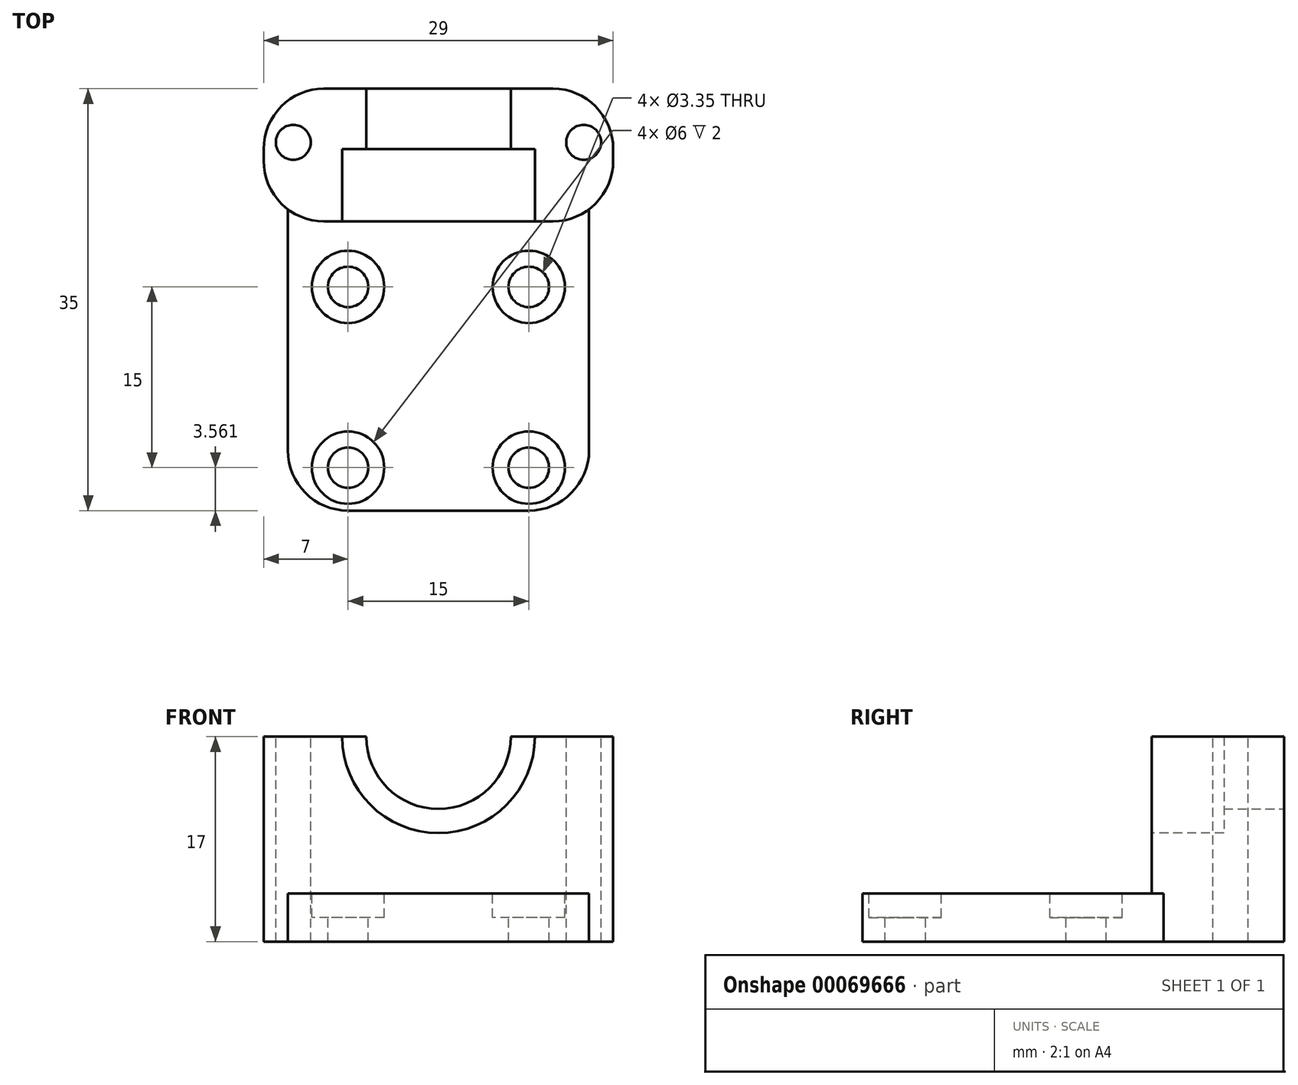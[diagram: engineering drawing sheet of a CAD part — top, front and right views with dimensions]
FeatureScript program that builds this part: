
annotation { "Feature Type Name" : "Feature", "Feature Type Description" : "" }
export const myFeature = defineFeature(function(context is Context, id is Id, definition is map)
    precondition{}
    {
        {
            var Q0;
            Q0=qCreatedBy(makeId("Top.planeOp"),FACE);
            var sketch = newSketch(context, id + "F0", { "sketchPlane" : qUnion([Q0])});
            skLineSegment(sketch, "E0.bottom", {"start": v(0, 0) * mm, "end": v(25, 0) * mm});
            skLineSegment(sketch, "E0.top", {"start": v(0, 35) * mm, "end": v(25, 35) * mm});
            skLineSegment(sketch, "E0.left", {"start": v(0, 0) * mm, "end": v(0, 35) * mm});
            skLineSegment(sketch, "E0.right", {"start": v(25, 0) * mm, "end": v(25, 35) * mm});
            skSolve(sketch);
        }
        {
            var Q0;
            Q0=qSketchRegion(id+"F0",true);
            extrude(context, id + "F1", {"entities" : qUnion([Q0]), "depth" : 4 * mm});
        }
        {
            var Q0;
            Q0=makeQuery(id+"F1.opExtrude","CAP_FACE",FACE,{"disambiguationData":[OSD([sQuery(id+"F0.wireOp",EDGE,"E0.bottom"),sQuery(id+"F0.wireOp",EDGE,"E0.top"),sQuery(id+"F0.wireOp",EDGE,"E0.left"),sQuery(id+"F0.wireOp",EDGE,"E0.right")])],"isStart":false});
            var sketch = newSketch(context, id + "F2", { "sketchPlane" : qUnion([Q0])});
            skCircle(sketch, "E1", {"center": v(5, 18.56) * mm, "radius": 1.68 * mm});
            skCircle(sketch, "E2", {"center": v(20, 18.56) * mm, "radius": 1.68 * mm});
            skCircle(sketch, "E3", {"center": v(5, 3.56) * mm, "radius": 1.68 * mm});
            skCircle(sketch, "E4", {"center": v(20, 3.56) * mm, "radius": 1.68 * mm});
            skLineSegment(sketch, "E5", {"start": v(5, 18.56) * mm, "end": v(0, 18.56) * mm});
            skLineSegment(sketch, "E6", {"start": v(20, 3.56) * mm, "end": v(25, 3.56) * mm});
            skCircle(sketch, "E7", {"center": v(5, 18.56) * mm, "radius": 3 * mm});
            skCircle(sketch, "E8", {"center": v(20, 18.56) * mm, "radius": 3 * mm});
            skCircle(sketch, "E9", {"center": v(5, 3.56) * mm, "radius": 3 * mm});
            skCircle(sketch, "E10", {"center": v(20, 3.56) * mm, "radius": 3 * mm});
            skSolve(sketch);
        }
        {
            var Q0;
            Q0=makeQuery(id+"F2.imprint","IMPRINT",FACE,{"disambiguationData":[TD([[makeQuery(id+"F2.imprint","IMPRINT",EDGE,{"derivedFrom":sQuery(id+"F2.wireOp",EDGE,"E1")}),1.0]])]});
            var Q1;
            Q1=makeQuery(id+"F2.imprint","IMPRINT",FACE,{"disambiguationData":[TD([[makeQuery(id+"F2.imprint","IMPRINT",EDGE,{"derivedFrom":sQuery(id+"F2.wireOp",EDGE,"E2")}),1.0]])]});
            var Q2;
            Q2=makeQuery(id+"F2.imprint","IMPRINT",FACE,{"disambiguationData":[TD([[makeQuery(id+"F2.imprint","IMPRINT",EDGE,{"derivedFrom":sQuery(id+"F2.wireOp",EDGE,"E4")}),1.0]])]});
            var Q3;
            Q3=makeQuery(id+"F2.imprint","IMPRINT",FACE,{"disambiguationData":[TD([[makeQuery(id+"F2.imprint","IMPRINT",EDGE,{"derivedFrom":sQuery(id+"F2.wireOp",EDGE,"E3")}),1.0]])]});
            extrude(context, id + "F3", {"entities" : qUnion([Q0, Q1, Q2, Q3]), "operationType" : NewBodyOperationType.REMOVE, "oppositeDirection" : true, "depth" : 25 * mm});
        }
        {
            var Q0;
            Q0=makeQuery(id+"F1.opExtrude","CAP_FACE",FACE,{"disambiguationData":[OSD([sQuery(id+"F0.wireOp",EDGE,"E0.bottom"),sQuery(id+"F0.wireOp",EDGE,"E0.top"),sQuery(id+"F0.wireOp",EDGE,"E0.left"),sQuery(id+"F0.wireOp",EDGE,"E0.right")])],"isStart":false});
            var sketch = newSketch(context, id + "F4", { "sketchPlane" : qUnion([Q0])});
            skLineSegment(sketch, "E11.bottom", {"start": v(0, 35) * mm, "end": v(25, 35) * mm});
            skLineSegment(sketch, "E11.top", {"start": v(0, 24) * mm, "end": v(25, 24) * mm});
            skLineSegment(sketch, "E11.left", {"start": v(0, 35) * mm, "end": v(0, 24) * mm});
            skLineSegment(sketch, "E11.right", {"start": v(25, 35) * mm, "end": v(25, 24) * mm});
            skSolve(sketch);
        }
        {
            var Q0;
            Q0=qSketchRegion(id+"F4",true);
            extrude(context, id + "F5", {"entities" : qUnion([Q0]), "operationType" : NewBodyOperationType.ADD, "depth" : 13 * mm});
        }
        {
            var Q0;
            Q0=makeQuery(id+"F5.boolean.opBoolean","MERGE",FACE,{"derivedFrom":[makeQuery(id+"F1.opExtrude","SWEPT_FACE",FACE,{"disambiguationData":[OSD([sQuery(id+"F0.wireOp",EDGE,"E0.top")])]}),makeQuery(id+"F5.opExtrude","SWEPT_FACE",FACE,{"disambiguationData":[OSD([sQuery(id+"F4.wireOp",EDGE,"E11.bottom")])]})]});
            var sketch = newSketch(context, id + "F6", { "sketchPlane" : qUnion([Q0])});
            skCircle(sketch, "E12", {"center": v(-12.5, 17) * mm, "radius": 6 * mm});
            skSolve(sketch);
        }
        {
            var Q0;
            {var subQ0=makeQuery(id+"F5.opExtrude","CAP_EDGE",EDGE,{"disambiguationData":[OSD([sQuery(id+"F4.wireOp",EDGE,"E11.bottom")])],"isStart":false});var subQ1=sQuery(id+"F6.wireOp",EDGE,"E12");var subQ3=makeQuery(id+"F6.imprint","INTERSECT",VERTEX,{"disambiguationData":[OD(0.0)],"derivedFrom":[subQ0,subQ1]});Q0=makeQuery(id+"F6.imprint","IMPRINT",FACE,{"disambiguationData":[TD([[makeQuery(id+"F6.imprint","IMPRINT",EDGE,{"disambiguationData":[TD([[subQ3,1.0]])],"derivedFrom":subQ1}),1.0]])]});}
            extrude(context, id + "F7", {"entities" : qUnion([Q0]), "operationType" : NewBodyOperationType.REMOVE, "oppositeDirection" : true, "depth" : 6 * mm});
        }
        {
            var Q0;
            Q0=makeQuery(id+"F5.opExtrude","SWEPT_FACE",FACE,{"disambiguationData":[OSD([sQuery(id+"F4.wireOp",EDGE,"E11.top")])]});
            var sketch = newSketch(context, id + "F8", { "sketchPlane" : qUnion([Q0])});
            skCircle(sketch, "E13", {"center": v(12.5, 17) * mm, "radius": 8 * mm});
            skSolve(sketch);
        }
        {
            var Q0;
            Q0=qSketchRegion(id+"F8",true);
            extrude(context, id + "F9", {"entities" : qUnion([Q0]), "operationType" : NewBodyOperationType.REMOVE, "oppositeDirection" : true, "depth" : 6 * mm});
        }
        {
            var Q0;
            Q0=makeQuery(id+"F2.imprint","IMPRINT",FACE,{"disambiguationData":[TD([[makeQuery(id+"F2.imprint","IMPRINT",EDGE,{"derivedFrom":sQuery(id+"F2.wireOp",EDGE,"E1")}),-1.0]])]});
            var Q1;
            Q1=makeQuery(id+"F2.imprint","IMPRINT",FACE,{"disambiguationData":[TD([[makeQuery(id+"F2.imprint","IMPRINT",EDGE,{"derivedFrom":sQuery(id+"F2.wireOp",EDGE,"E2")}),-1.0]])]});
            var Q2;
            Q2=makeQuery(id+"F2.imprint","IMPRINT",FACE,{"disambiguationData":[TD([[makeQuery(id+"F2.imprint","IMPRINT",EDGE,{"derivedFrom":sQuery(id+"F2.wireOp",EDGE,"E4")}),-1.0]])]});
            var Q3;
            Q3=makeQuery(id+"F2.imprint","IMPRINT",FACE,{"disambiguationData":[TD([[makeQuery(id+"F2.imprint","IMPRINT",EDGE,{"derivedFrom":sQuery(id+"F2.wireOp",EDGE,"E3")}),-1.0]])]});
            extrude(context, id + "F10", {"entities" : qUnion([Q0, Q1, Q2, Q3]), "operationType" : NewBodyOperationType.REMOVE, "oppositeDirection" : true, "depth" : 2 * mm});
        }
        {
            var Q0;
            Q0=makeQuery(id+"F1.opExtrude","SWEPT_EDGE",EDGE,{"disambiguationData":[OSD([sQuery(id+"F0.wireOp",EDGE,"E0.bottom"),sQuery(id+"F0.wireOp",EDGE,"E0.left")])]});
            var Q1;
            Q1=makeQuery(id+"F1.opExtrude","SWEPT_EDGE",EDGE,{"disambiguationData":[OSD([sQuery(id+"F0.wireOp",EDGE,"E0.bottom"),sQuery(id+"F0.wireOp",EDGE,"E0.right")])]});
            fillet(context, id + "F11", {"entities" : qUnion([Q0, Q1]), "radius" : 5 * mm, "tangentPropagation" : true, "allowEdgeOverflow" : false});
        }
        {
            var Q0;
            Q0=makeQuery(id+"F5.boolean.opBoolean","MERGE",FACE,{"derivedFrom":[makeQuery(id+"F1.opExtrude","SWEPT_FACE",FACE,{"disambiguationData":[OSD([sQuery(id+"F0.wireOp",EDGE,"E0.left")])]}),makeQuery(id+"F5.opExtrude","SWEPT_FACE",FACE,{"disambiguationData":[OSD([sQuery(id+"F4.wireOp",EDGE,"E11.left")])]})]});
            var sketch = newSketch(context, id + "F12", { "sketchPlane" : qUnion([Q0])});
            skLineSegment(sketch, "E14.bottom", {"start": v(-35, 0) * mm, "end": v(-24, 0) * mm});
            skLineSegment(sketch, "E14.top", {"start": v(-35, 17) * mm, "end": v(-24, 17) * mm});
            skLineSegment(sketch, "E14.left", {"start": v(-35, 0) * mm, "end": v(-35, 17) * mm});
            skLineSegment(sketch, "E14.right", {"start": v(-24, 0) * mm, "end": v(-24, 17) * mm});
            skSolve(sketch);
        }
        {
            var Q0;
            {var subQ3=sQuery(id+"F12.wireOp",EDGE,"E14.bottom");Q0=makeQuery(id+"F12.imprint","IMPRINT",FACE,{"disambiguationData":[TD([[makeQuery(id+"F12.imprint","IMPRINT",EDGE,{"derivedFrom":subQ3}),-1.0]])]});}
            var Q1;
            Q1=makeQuery(id+"F5.boolean.opBoolean","MERGE",FACE,{"derivedFrom":[makeQuery(id+"F1.opExtrude","SWEPT_FACE",FACE,{"disambiguationData":[OSD([sQuery(id+"F0.wireOp",EDGE,"E0.right")])]}),makeQuery(id+"F5.opExtrude","SWEPT_FACE",FACE,{"disambiguationData":[OSD([sQuery(id+"F4.wireOp",EDGE,"E11.right")])]})]});
            extrude(context, id + "F13", {"entities" : qUnion([Q0, Q1]), "operationType" : NewBodyOperationType.ADD, "depth" : 2 * mm});
        }
        {
            var Q0;
            Q0=makeQuery(id+"F5.boolean.opBoolean","MERGE",FACE,{"derivedFrom":[makeQuery(id+"F1.opExtrude","SWEPT_FACE",FACE,{"disambiguationData":[OSD([sQuery(id+"F0.wireOp",EDGE,"E0.right")])]}),makeQuery(id+"F5.opExtrude","SWEPT_FACE",FACE,{"disambiguationData":[OSD([sQuery(id+"F4.wireOp",EDGE,"E11.right")])]})]});
            var sketch = newSketch(context, id + "F14", { "sketchPlane" : qUnion([Q0])});
            skLineSegment(sketch, "E15.bottom", {"start": v(35, 0) * mm, "end": v(24, 0) * mm});
            skLineSegment(sketch, "E15.top", {"start": v(35, 17) * mm, "end": v(24, 17) * mm});
            skLineSegment(sketch, "E15.left", {"start": v(35, 0) * mm, "end": v(35, 17) * mm});
            skLineSegment(sketch, "E15.right", {"start": v(24, 0) * mm, "end": v(24, 17) * mm});
            skSolve(sketch);
        }
        {
            var Q0;
            Q0=qSketchRegion(id+"F14",true);
            extrude(context, id + "F15", {"entities" : qUnion([Q0]), "operationType" : NewBodyOperationType.ADD, "depth" : 2 * mm});
        }
        {
            var Q0;
            {var subQ0=sQuery(id+"F4.wireOp",EDGE,"E11.bottom");var subQ1=sQuery(id+"F4.wireOp",EDGE,"E11.top");var subQ2=sQuery(id+"F4.wireOp",EDGE,"E11.left");Q0=makeQuery(id+"F9.boolean.opBoolean","SPLIT",FACE,{"disambiguationData":[TD([makeQuery(id+"F1.opExtrude","SWEPT_FACE",FACE,{"disambiguationData":[OSD([sQuery(id+"F0.wireOp",EDGE,"E0.left")])]})])],"derivedFrom":makeQuery(id+"F5.opExtrude","CAP_FACE",FACE,{"disambiguationData":[OSD([subQ0,subQ1,subQ2,sQuery(id+"F4.wireOp",EDGE,"E11.right")])],"isStart":false})});}
            var sketch = newSketch(context, id + "F16", { "sketchPlane" : qUnion([Q0])});
            skCircle(sketch, "E16", {"center": v(0.45, 30.55) * mm, "radius": 1.45 * mm});
            skCircle(sketch, "E17", {"center": v(24.55, 30.55) * mm, "radius": 1.45 * mm});
            skSolve(sketch);
        }
        {
            var Q0;
            Q0=qSketchRegion(id+"F16",true);
            extrude(context, id + "F17", {"entities" : qUnion([Q0]), "operationType" : NewBodyOperationType.REMOVE, "oppositeDirection" : true, "depth" : 25 * mm});
        }
        {
            var Q0;
            Q0=makeQuery(id+"F13.opExtrude","CAP_EDGE",EDGE,{"disambiguationData":[OSD([sQuery(id+"F12.wireOp",EDGE,"E14.right")])],"isStart":false});
            var Q1;
            Q1=makeQuery(id+"F13.opExtrude","CAP_EDGE",EDGE,{"disambiguationData":[OSD([sQuery(id+"F12.wireOp",EDGE,"E14.left")])],"isStart":false});
            var Q2;
            Q2=makeQuery(id+"F15.opExtrude","CAP_EDGE",EDGE,{"disambiguationData":[OSD([sQuery(id+"F14.wireOp",EDGE,"E15.left")])],"isStart":false});
            var Q3;
            Q3=makeQuery(id+"F15.opExtrude","CAP_EDGE",EDGE,{"disambiguationData":[OSD([sQuery(id+"F14.wireOp",EDGE,"E15.right")])],"isStart":false});
            fillet(context, id + "F18", {"entities" : qUnion([Q0, Q1, Q2, Q3]), "radius" : 5 * mm, "tangentPropagation" : true, "allowEdgeOverflow" : false});
        }
    });
